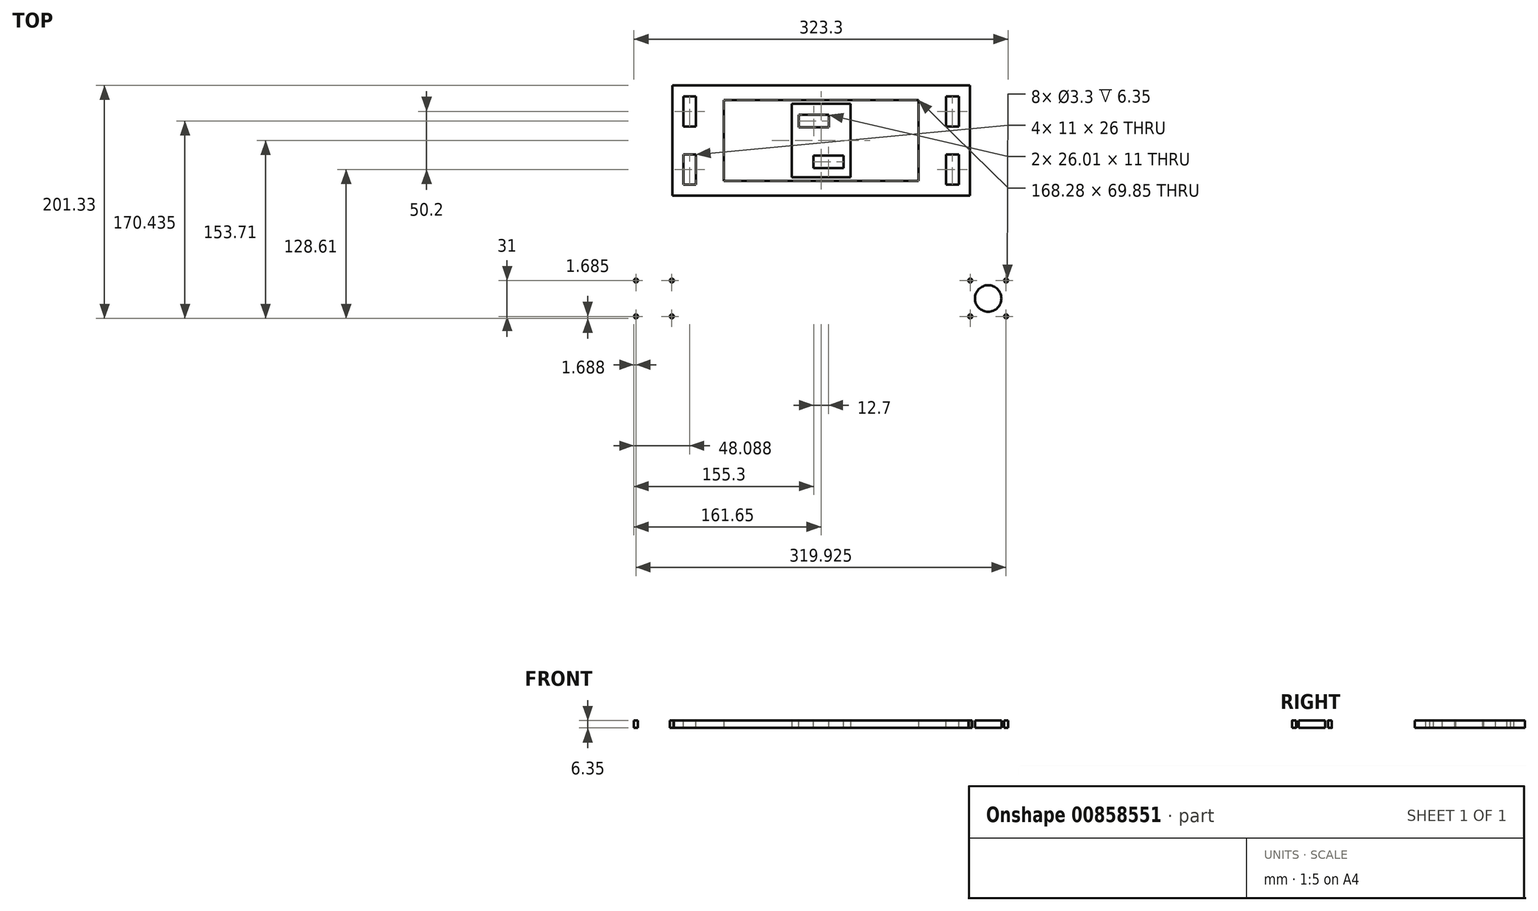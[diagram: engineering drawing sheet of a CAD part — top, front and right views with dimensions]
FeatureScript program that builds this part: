
annotation { "Feature Type Name" : "Feature", "Feature Type Description" : "" }
export const myFeature = defineFeature(function(context is Context, id is Id, definition is map)
    precondition{}
    {
        {
            var Q0;
            Q0=qCreatedBy(makeId("Top.planeOp"),FACE);
            var sketch = newSketch(context, id + "F0", { "sketchPlane" : qUnion([Q0])});
            skLineSegment(sketch, "E0.bottom", {"start": v(25.4, 31.75) * mm, "end": v(-25.4, 31.75) * mm});
            skLineSegment(sketch, "E0.top", {"start": v(25.4, -31.75) * mm, "end": v(-25.4, -31.75) * mm});
            skLineSegment(sketch, "E0.left", {"start": v(25.4, 31.75) * mm, "end": v(25.4, -31.75) * mm});
            skLineSegment(sketch, "E0.right", {"start": v(-25.4, 31.75) * mm, "end": v(-25.4, -31.75) * mm});
            skPoint(sketch, "E0.middle", {"position": v(0, 0) * mm});
            skLineSegment(sketch, "E1.bottom", {"start": v(128.59, 47.63) * mm, "end": v(-128.59, 47.62) * mm});
            skLineSegment(sketch, "E1.top", {"start": v(128.59, -47.62) * mm, "end": v(-128.59, -47.63) * mm});
            skLineSegment(sketch, "E1.left", {"start": v(128.59, 47.63) * mm, "end": v(128.59, -47.62) * mm});
            skLineSegment(sketch, "E1.right", {"start": v(-128.59, 47.62) * mm, "end": v(-128.59, -47.63) * mm});
            skLineSegment(sketch, "E2.0", {"start": v(84.14, 34.93) * mm, "end": v(-84.14, 34.92) * mm});
            skLineSegment(sketch, "E3.0", {"start": v(84.14, -34.92) * mm, "end": v(-84.14, -34.93) * mm});
            skLineSegment(sketch, "E4.trimOffspring", {"start": v(-84.14, 34.92) * mm, "end": v(-84.14, -34.93) * mm});
            skLineSegment(sketch, "E5.trimOffspring", {"start": v(84.14, 34.93) * mm, "end": v(84.14, -34.92) * mm});
            skLineSegment(sketch, "E6.bottom", {"start": v(-131.76, 107.95) * mm, "end": v(131.76, 107.95) * mm});
            skLineSegment(sketch, "E6.top", {"start": v(-131.76, -107.95) * mm, "end": v(131.76, -107.95) * mm});
            skLineSegment(sketch, "E6.left", {"start": v(-131.76, 107.95) * mm, "end": v(-131.76, -107.95) * mm});
            skLineSegment(sketch, "E6.right", {"start": v(131.76, 107.95) * mm, "end": v(131.76, -107.95) * mm});
            skLineSegment(sketch, "E7.bottom", {"start": v(-173.04, 136.53) * mm, "end": v(173.04, 136.53) * mm});
            skLineSegment(sketch, "E7.top", {"start": v(-173.04, -136.53) * mm, "end": v(173.04, -136.53) * mm});
            skLineSegment(sketch, "E7.left", {"start": v(-173.04, 136.53) * mm, "end": v(-173.04, -161.93) * mm});
            skLineSegment(sketch, "E7.right", {"start": v(173.04, 136.53) * mm, "end": v(173.04, -161.93) * mm});
            skLineSegment(sketch, "E8.0", {"start": v(-173.04, -161.93) * mm, "end": v(173.04, -161.93) * mm});
            skSolve(sketch);
        }
        {
            var Q0;
            Q0=makeQuery(id+"F0.imprint","IMPRINT",FACE,{"disambiguationData":[TD([[makeQuery(id+"F0.imprint","IMPRINT",EDGE,{"derivedFrom":sQuery(id+"F0.wireOp",EDGE,"E1.bottom")}),1.0]])]});
            extrude(context, id + "F1", {"entities" : qUnion([Q0]), "depth" : 6.35 * mm, "offsetDistance" : 25.4 * mm});
        }
        {
            var Q0;
            Q0=makeQuery(id+"F0.imprint","IMPRINT",FACE,{"disambiguationData":[TD([[makeQuery(id+"F0.imprint","IMPRINT",EDGE,{"derivedFrom":sQuery(id+"F0.wireOp",EDGE,"E0.bottom")}),1.0]])]});
            extrude(context, id + "F2", {"entities" : qUnion([Q0]), "depth" : 6.35 * mm, "offsetDistance" : 25.4 * mm});
        }
        {
            var Q0;
            Q0=makeQuery(id+"F0.imprint","IMPRINT",FACE,{"disambiguationData":[TD([[makeQuery(id+"F0.imprint","IMPRINT",EDGE,{"derivedFrom":sQuery(id+"F0.wireOp",EDGE,"E6.bottom")}),1.0]])]});
            var Q1;
            {var subQ0=sQuery(id+"F0.wireOp",EDGE,"E7.top");Q1=makeQuery(id+"F0.imprint","IMPRINT",FACE,{"disambiguationData":[TD([[makeQuery(id+"F0.imprint","IMPRINT",EDGE,{"derivedFrom":subQ0}),-1.0]])]});}
            extrude(context, id + "F3", {"entities" : qUnion([Q0, Q1]), "depth" : 6.35 * mm, "offsetDistance" : 25.4 * mm});
        }
        {
            var Q0;
            Q0=makeQuery(id+"F3.opExtrude","CAP_FACE",FACE,{"disambiguationData":[OSD([sQuery(id+"F0.wireOp",EDGE,"E6.bottom"),sQuery(id+"F0.wireOp",EDGE,"E6.top"),sQuery(id+"F0.wireOp",EDGE,"E6.left"),sQuery(id+"F0.wireOp",EDGE,"E6.right"),sQuery(id+"F0.wireOp",EDGE,"E7.bottom"),sQuery(id+"F0.wireOp",EDGE,"E7.left"),sQuery(id+"F0.wireOp",EDGE,"E7.right"),sQuery(id+"F0.wireOp",EDGE,"E8.0")])],"isStart":false});
            var sketch = newSketch(context, id + "F4", { "sketchPlane" : qUnion([Q0])});
            skCircle(sketch, "E9", {"center": v(-144.46, -136.53) * mm, "radius": 11.43 * mm});
            skCircle(sketch, "E10", {"center": v(-128.96, -121.03) * mm, "radius": 1.69 * mm});
            skCircle(sketch, "E11.1.0", {"center": v(-159.96, -121.02) * mm, "radius": 1.69 * mm});
            skCircle(sketch, "E11.2.0", {"center": v(-159.96, -152.02) * mm, "radius": 1.69 * mm});
            skCircle(sketch, "E11.3.0", {"center": v(-128.97, -152.03) * mm, "radius": 1.69 * mm});
            skLineSegment(sketch, "E12", {"start": v(0, -161.92) * mm, "end": v(0, 136.53) * mm, "construction": true});
            skPoint(sketch, "E13.MirrorP", {"position": v(144.46, -136.53) * mm});
            skCircle(sketch, "E14.MirrorC", {"center": v(128.96, -121.03) * mm, "radius": 1.69 * mm});
            skCircle(sketch, "E15.MirrorC", {"center": v(159.96, -121.02) * mm, "radius": 1.69 * mm});
            skCircle(sketch, "E16.MirrorC", {"center": v(159.96, -152.02) * mm, "radius": 1.69 * mm});
            skCircle(sketch, "E17.MirrorC", {"center": v(128.97, -152.03) * mm, "radius": 1.69 * mm});
            skCircle(sketch, "E18.MirrorC", {"center": v(144.46, -136.53) * mm, "radius": 11.43 * mm});
            skSolve(sketch);
        }
        {
            var Q0;
            Q0=makeQuery(id+"F4.imprint","IMPRINT",FACE,{"disambiguationData":[TD([[makeQuery(id+"F4.imprint","IMPRINT",EDGE,{"derivedFrom":sQuery(id+"F4.wireOp",EDGE,"E9")}),1.0]])]});
            var Q1;
            Q1=makeQuery(id+"F4.imprint","IMPRINT",FACE,{"disambiguationData":[TD([[makeQuery(id+"F4.imprint","IMPRINT",EDGE,{"derivedFrom":sQuery(id+"F4.wireOp",EDGE,"E18.MirrorC")}),-1.0]])]});
            var Q2;
            Q2=sQuery(id+"F0.wireOp",EDGE,"E6.top");
            var Q3;
            Q3=sQuery(id+"F0.wireOp",EDGE,"E8.0");
            var Q4;
            Q4=sQuery(id+"F4.wireOp",EDGE,"E9");
            extrude(context, id + "F5", {"entities" : qUnion([Q0, Q1]), "operationType" : NewBodyOperationType.REMOVE, "surfaceEntities" : qUnion([Q2, Q3, Q4]), "oppositeDirection" : true, "depth" : 25.4 * mm, "offsetDistance" : 25.4 * mm});
        }
        {
            var Q0;
            Q0=sQuery(id+"F4.wireOp",VERTEX,"E11.1.0.center");
            var Q1;
            Q1=sQuery(id+"F4.wireOp",VERTEX,"E10.center");
            var Q2;
            Q2=sQuery(id+"F4.wireOp",VERTEX,"E11.3.0.center");
            var Q3;
            Q3=sQuery(id+"F4.wireOp",VERTEX,"E11.2.0.center");
            var Q4;
            Q4=sQuery(id+"F4.wireOp",VERTEX,"E14.MirrorC.center");
            var Q5;
            Q5=sQuery(id+"F4.wireOp",VERTEX,"E15.MirrorC.center");
            var Q6;
            Q6=sQuery(id+"F4.wireOp",VERTEX,"E17.MirrorC.center");
            var Q7;
            Q7=sQuery(id+"F4.wireOp",VERTEX,"E16.MirrorC.center");
            var Q8;
            Q8=makeQuery(id+"F3.opExtrude","SWEPT_BODY",BODY,{"disambiguationData":[OSD([sQuery(id+"F0.wireOp",EDGE,"E6.bottom"),sQuery(id+"F0.wireOp",EDGE,"E6.top"),sQuery(id+"F0.wireOp",EDGE,"E6.left"),sQuery(id+"F0.wireOp",EDGE,"E6.right"),sQuery(id+"F0.wireOp",EDGE,"E7.bottom"),sQuery(id+"F0.wireOp",EDGE,"E7.left"),sQuery(id+"F0.wireOp",EDGE,"E7.right"),sQuery(id+"F0.wireOp",EDGE,"E8.0")])]});
            hole(context, id + "F6", {"style" : HoleStyle.SIMPLE, "endStyle" : HoleEndStyle.THROUGH, "standardTappedOrClearance" : lookupTablePath({ "fit" : "Normal", "standard" : "ISO", "size" : "M3", "type" : "Clearance" }), "standardBlindInLast" : lookupTablePath({ "fit" : "Standard", "standard" : "ISO", "size" : "M3", "type" : "Clearance" }), "holeDiameter" : 3.3 * mm, "majorDiameter" : 6.35 * mm, "isTappedThrough" : true, "tappedDepth" : 12.7 * mm, "tapClearance" : 3, "locations" : qUnion([Q0, Q1, Q2, Q3, Q4, Q5, Q6, Q7]), "scope" : qUnion([Q8])});
        }
        {
            var Q0;
            Q0=makeQuery(id+"F4.imprint","IMPRINT",FACE,{"disambiguationData":[TD([[makeQuery(id+"F4.imprint","IMPRINT",EDGE,{"derivedFrom":makeQuery(id+"F3.opExtrude","CAP_EDGE",EDGE,{"disambiguationData":[OSD([sQuery(id+"F0.wireOp",EDGE,"E6.bottom")])],"isStart":false})}),-1.0]])]});
            var sketch = newSketch(context, id + "F7", { "sketchPlane" : qUnion([Q0])});
            skLineSegment(sketch, "E19.bottom", {"start": v(-119.06, 38.1) * mm, "end": v(-108.06, 38.1) * mm});
            skLineSegment(sketch, "E19.top", {"start": v(-119.06, 12.1) * mm, "end": v(-108.06, 12.1) * mm});
            skLineSegment(sketch, "E19.left", {"start": v(-119.06, 38.1) * mm, "end": v(-119.06, 12.1) * mm});
            skLineSegment(sketch, "E19.right", {"start": v(-108.06, 38.1) * mm, "end": v(-108.06, 12.1) * mm});
            skLineSegment(sketch, "E20.MirrorCS", {"start": v(108.06, 38.1) * mm, "end": v(108.06, 12.1) * mm});
            skLineSegment(sketch, "E21.MirrorCS", {"start": v(119.06, 38.1) * mm, "end": v(119.06, 12.1) * mm});
            skLineSegment(sketch, "E22.MirrorCS", {"start": v(119.06, 12.1) * mm, "end": v(108.06, 12.1) * mm});
            skLineSegment(sketch, "E23.MirrorCS", {"start": v(119.06, 38.1) * mm, "end": v(108.06, 38.1) * mm});
            skLineSegment(sketch, "E24", {"start": v(-183.3, 0) * mm, "end": v(191.16, 0) * mm, "construction": true});
            skLineSegment(sketch, "E25.MirrorCS", {"start": v(-119.06, -12.1) * mm, "end": v(-108.06, -12.1) * mm});
            skLineSegment(sketch, "E26.MirrorCS", {"start": v(-119.06, -38.1) * mm, "end": v(-108.06, -38.1) * mm});
            skLineSegment(sketch, "E27.MirrorCS", {"start": v(-108.06, -38.1) * mm, "end": v(-108.06, -12.1) * mm});
            skLineSegment(sketch, "E28.MirrorCS", {"start": v(-119.06, -38.1) * mm, "end": v(-119.06, -12.1) * mm});
            skLineSegment(sketch, "E29.MirrorCS", {"start": v(119.06, -38.1) * mm, "end": v(108.06, -38.1) * mm});
            skLineSegment(sketch, "E30.MirrorCS", {"start": v(119.06, -12.1) * mm, "end": v(108.06, -12.1) * mm});
            skLineSegment(sketch, "E31.MirrorCS", {"start": v(119.06, -38.1) * mm, "end": v(119.06, -12.1) * mm});
            skLineSegment(sketch, "E32.MirrorCS", {"start": v(108.06, -38.1) * mm, "end": v(108.06, -12.1) * mm});
            skLineSegment(sketch, "E33.bottom", {"start": v(-19.35, 22.22) * mm, "end": v(6.65, 22.23) * mm});
            skLineSegment(sketch, "E33.top", {"start": v(-19.35, 11.23) * mm, "end": v(6.65, 11.23) * mm});
            skLineSegment(sketch, "E33.left", {"start": v(-19.35, 22.23) * mm, "end": v(-19.35, 11.23) * mm});
            skLineSegment(sketch, "E33.right", {"start": v(6.65, 22.23) * mm, "end": v(6.65, 11.23) * mm});
            skLineSegment(sketch, "E34", {"start": v(-6.35, 22.23) * mm, "end": v(-6.35, 11.23) * mm, "construction": true});
            skLineSegment(sketch, "E35.bottom", {"start": v(-6.65, -12.94) * mm, "end": v(19.35, -12.94) * mm});
            skLineSegment(sketch, "E35.top", {"start": v(-6.65, -23.94) * mm, "end": v(19.35, -23.94) * mm});
            skLineSegment(sketch, "E35.left", {"start": v(-6.65, -12.94) * mm, "end": v(-6.65, -23.94) * mm});
            skLineSegment(sketch, "E35.right", {"start": v(19.35, -12.94) * mm, "end": v(19.35, -23.94) * mm});
            skLineSegment(sketch, "E36", {"start": v(6.35, -12.94) * mm, "end": v(6.35, -23.94) * mm, "construction": true});
            skSolve(sketch);
        }
        {
            var Q0;
            Q0=makeQuery(id+"F7.imprint","IMPRINT",FACE,{"disambiguationData":[TD([[makeQuery(id+"F7.imprint","IMPRINT",EDGE,{"derivedFrom":sQuery(id+"F7.wireOp",EDGE,"E25.MirrorCS")}),-1.0]])]});
            var Q1;
            Q1=makeQuery(id+"F7.imprint","IMPRINT",FACE,{"disambiguationData":[TD([[makeQuery(id+"F7.imprint","IMPRINT",EDGE,{"derivedFrom":sQuery(id+"F7.wireOp",EDGE,"E19.bottom")}),-1.0]])]});
            var Q2;
            Q2=makeQuery(id+"F7.imprint","IMPRINT",FACE,{"disambiguationData":[TD([[makeQuery(id+"F7.imprint","IMPRINT",EDGE,{"derivedFrom":sQuery(id+"F7.wireOp",EDGE,"E33.bottom")}),-1.0]])]});
            var Q3;
            Q3=makeQuery(id+"F7.imprint","IMPRINT",FACE,{"disambiguationData":[TD([[makeQuery(id+"F7.imprint","IMPRINT",EDGE,{"derivedFrom":sQuery(id+"F7.wireOp",EDGE,"E29.MirrorCS")}),-1.0]])]});
            var Q4;
            Q4=makeQuery(id+"F7.imprint","IMPRINT",FACE,{"disambiguationData":[TD([[makeQuery(id+"F7.imprint","IMPRINT",EDGE,{"derivedFrom":sQuery(id+"F7.wireOp",EDGE,"E20.MirrorCS")}),1.0]])]});
            var Q5;
            Q5=makeQuery(id+"F7.imprint","IMPRINT",FACE,{"disambiguationData":[TD([[makeQuery(id+"F7.imprint","IMPRINT",EDGE,{"derivedFrom":sQuery(id+"F7.wireOp",EDGE,"E35.bottom")}),-1.0]])]});
            extrude(context, id + "F8", {"entities" : qUnion([Q0, Q1, Q2, Q3, Q4, Q5]), "operationType" : NewBodyOperationType.REMOVE, "oppositeDirection" : true, "depth" : 25.4 * mm, "offsetDistance" : 25.4 * mm});
        }
    });
